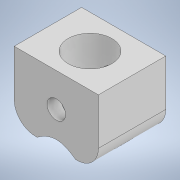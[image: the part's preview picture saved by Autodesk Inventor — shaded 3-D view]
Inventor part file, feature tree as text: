
AUTODESK INVENTOR PART (.ipt)
format: ipt  version: 2022 (Build 260153000, 153)  size: 168,960 bytes
history: native  units: mm
features: extrude x4, sketch x4, chamfer x1, fillet x1
ambient origin geometry x8: Origin, YZ Plane, XZ Plane, XY Plane, X Axis, Y Axis, Z Axis, Center Point
bodies: Solid1 (feature_tree)
feature tree (10):
  extrude  "Extrusion1"  Depth=10.0mm
  extrude  "Extrusion2"  Depth=8.0mm
  chamfer  "Chamfer1"  [1 undecoded]
  extrude  "Extrusion3"  Depth=2.2mm
  fillet  "Fillet1"  [1 undecoded]
  extrude  "Extrusion4"  Depth=8.0mm
  sketch  "Sketch1"  dims[d0=10.0mm d1=10.0mm]
  sketch  "Sketch2"  dims[d2=8.0mm d3=0.0mm d4=5.2mm d5=0.0mm d6=0.0mm]
  sketch  "Sketch3"  dims[d7=2.0mm d8=3.0mm d9=45.0deg d10=2.2mm d11=0.0mm d12=0.0mm]
  sketch  "Sketch4"  dims[d13=2.5mm d14=3.0mm d15=8.0mm d16=0.0mm d17=0.0mm d18=8.0mm]
note: 2 required parameter values undecoded (feature->parameter linkage not recoverable at this tier; creation-order binding heuristic only, values carry confidence <= 0.55)
